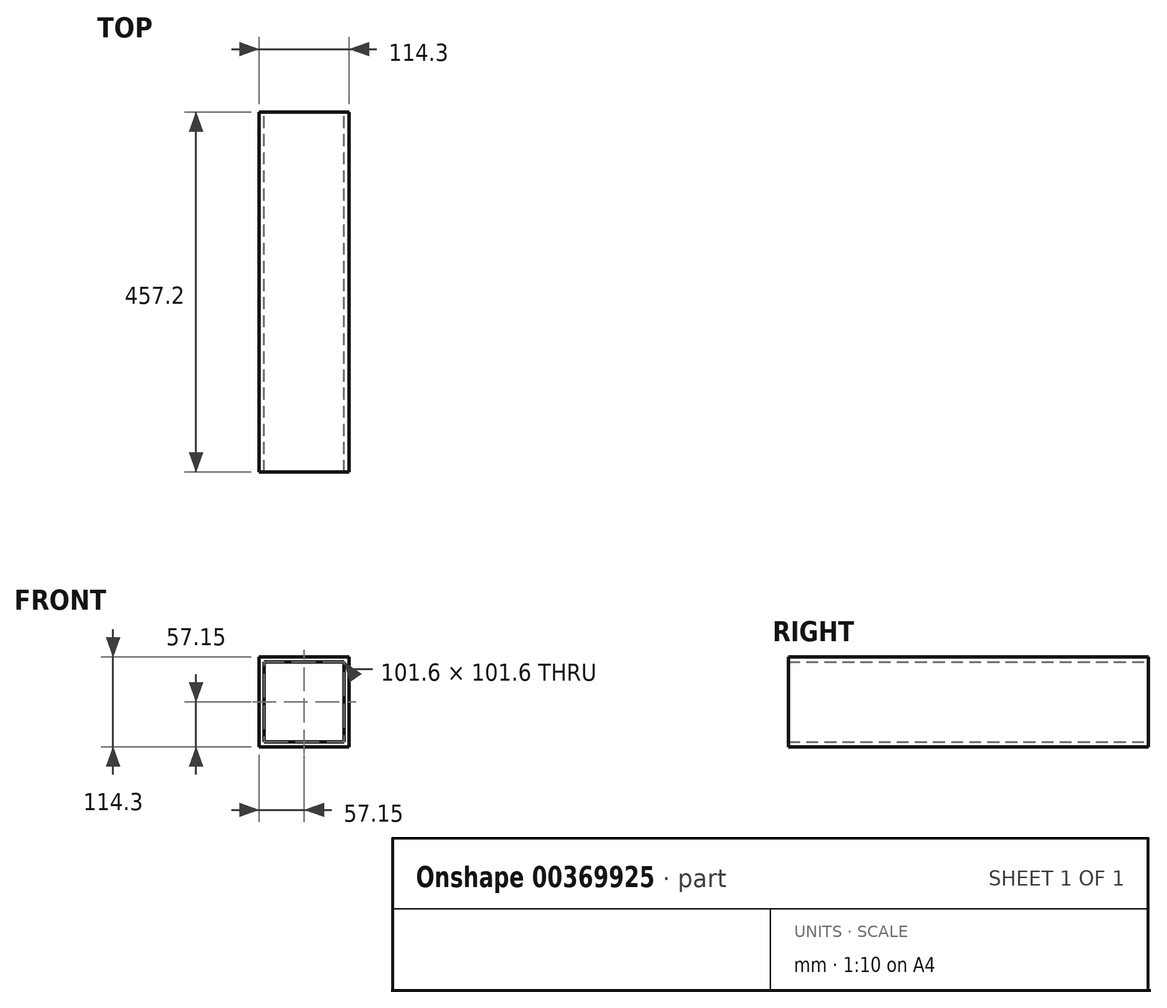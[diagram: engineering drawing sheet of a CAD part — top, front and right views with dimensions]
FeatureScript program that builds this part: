
annotation { "Feature Type Name" : "Feature", "Feature Type Description" : "" }
export const myFeature = defineFeature(function(context is Context, id is Id, definition is map)
    precondition{}
    {
        {
            var Q0;
            Q0=qCreatedBy(makeId("Front.planeOp"),FACE);
            var sketch = newSketch(context, id + "F0", { "sketchPlane" : qUnion([Q0])});
            skLineSegment(sketch, "E0.bottom", {"start": v(0, 0) * mm, "end": v(114.3, 0) * mm});
            skLineSegment(sketch, "E0.top", {"start": v(0, 114.3) * mm, "end": v(114.3, 114.3) * mm});
            skLineSegment(sketch, "E0.left", {"start": v(0, 0) * mm, "end": v(0, 114.3) * mm});
            skLineSegment(sketch, "E0.right", {"start": v(114.3, 0) * mm, "end": v(114.3, 114.3) * mm});
            skLineSegment(sketch, "E1.bottom", {"start": v(6.35, 107.95) * mm, "end": v(107.95, 107.95) * mm});
            skLineSegment(sketch, "E1.top", {"start": v(6.35, 6.35) * mm, "end": v(107.95, 6.35) * mm});
            skLineSegment(sketch, "E1.left", {"start": v(6.35, 107.95) * mm, "end": v(6.35, 6.35) * mm});
            skLineSegment(sketch, "E1.right", {"start": v(107.95, 107.95) * mm, "end": v(107.95, 6.35) * mm});
            skSolve(sketch);
        }
        {
            var Q0;
            Q0 = qSketchRegion(id + "F0", true);
            extrude(context, id + "F1", {"entities" : qUnion([Q0]), "depth" : 457.2 * mm});
        }
    });
